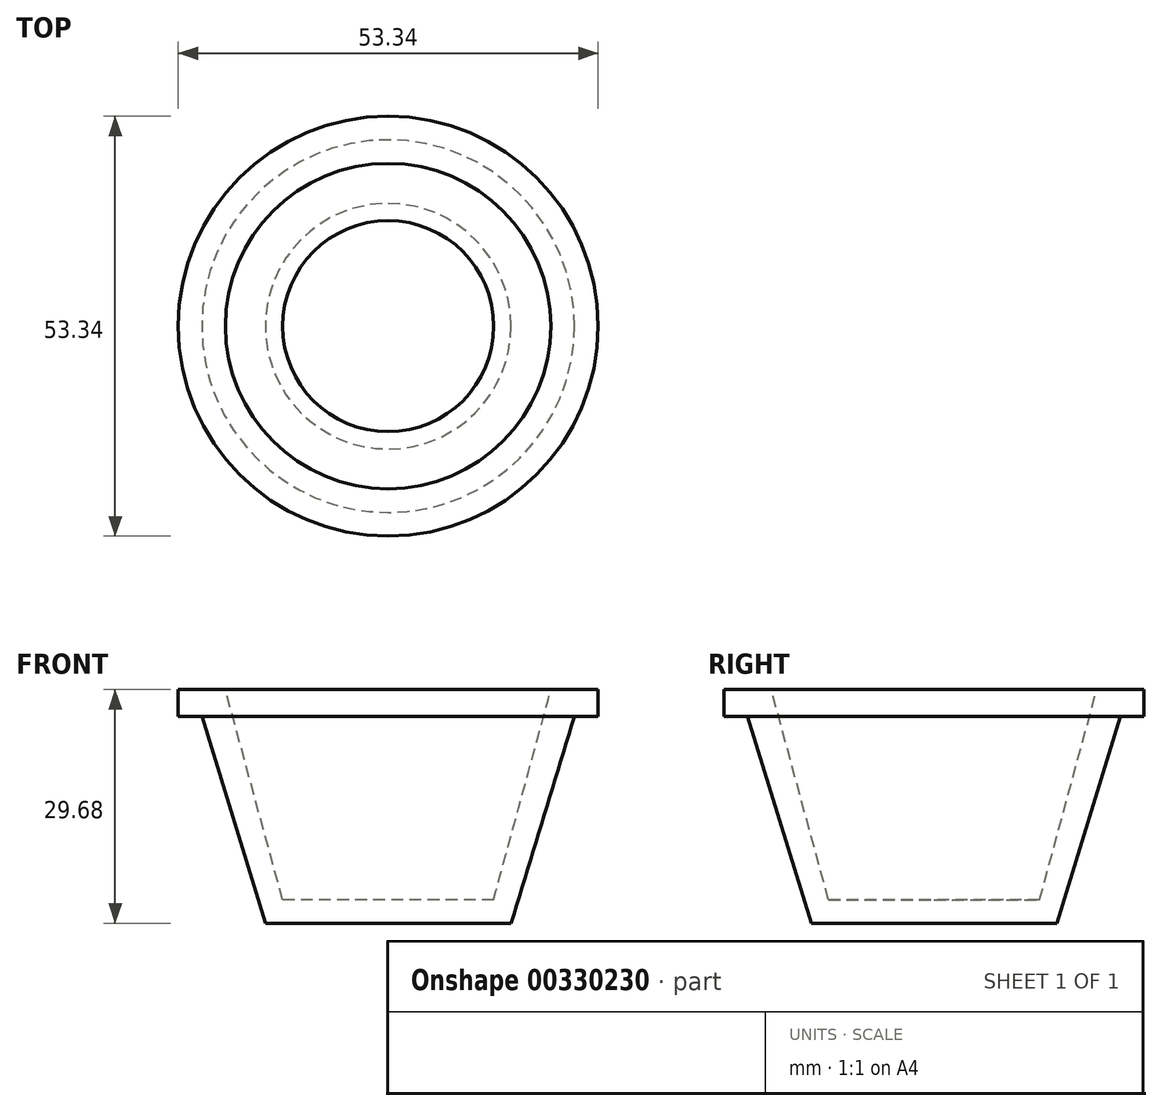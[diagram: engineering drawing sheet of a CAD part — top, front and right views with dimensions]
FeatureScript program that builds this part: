
annotation { "Feature Type Name" : "Feature", "Feature Type Description" : "" }
export const myFeature = defineFeature(function(context is Context, id is Id, definition is map)
    precondition{}
    {
        {
            var Q0;
            Q0=qCreatedBy(makeId("Front.planeOp"),FACE);
            var sketch = newSketch(context, id + "F0", { "sketchPlane" : qUnion([Q0])});
            skLineSegment(sketch, "E0", {"start": v(0, 0) * mm, "end": v(15.6, 0) * mm});
            skLineSegment(sketch, "E1", {"start": v(15.6, 0) * mm, "end": v(23.67, 26.3) * mm});
            skLineSegment(sketch, "E2", {"start": v(23.67, 26.3) * mm, "end": v(26.67, 26.3) * mm});
            skLineSegment(sketch, "E3", {"start": v(26.67, 26.3) * mm, "end": v(26.67, 29.68) * mm});
            skLineSegment(sketch, "E4", {"start": v(26.67, 29.68) * mm, "end": v(20.67, 29.68) * mm});
            skLineSegment(sketch, "E5", {"start": v(20.67, 29.68) * mm, "end": v(13.4, 3) * mm});
            skLineSegment(sketch, "E6", {"start": v(13.4, 3) * mm, "end": v(0, 3) * mm});
            skLineSegment(sketch, "E7", {"start": v(0, 3) * mm, "end": v(0, 0) * mm});
            skSolve(sketch);
        }
        {
            var Q0;
            Q0=makeQuery(id+"F0.imprint","IMPRINT",FACE,{"disambiguationData":[TD([[makeQuery(id+"F0.imprint","IMPRINT",EDGE,{"derivedFrom":sQuery(id+"F0.wireOp",EDGE,"E0")}),1.0]])]});
            var Q1;
            Q1=sQuery(id+"F0.wireOp",EDGE,"E7");
            revolve(context, id + "F1", {"entities" : qUnion([Q0]), "axis" : qUnion([Q1]), "revolveType" : RevolveType.FULL});
        }
    });
